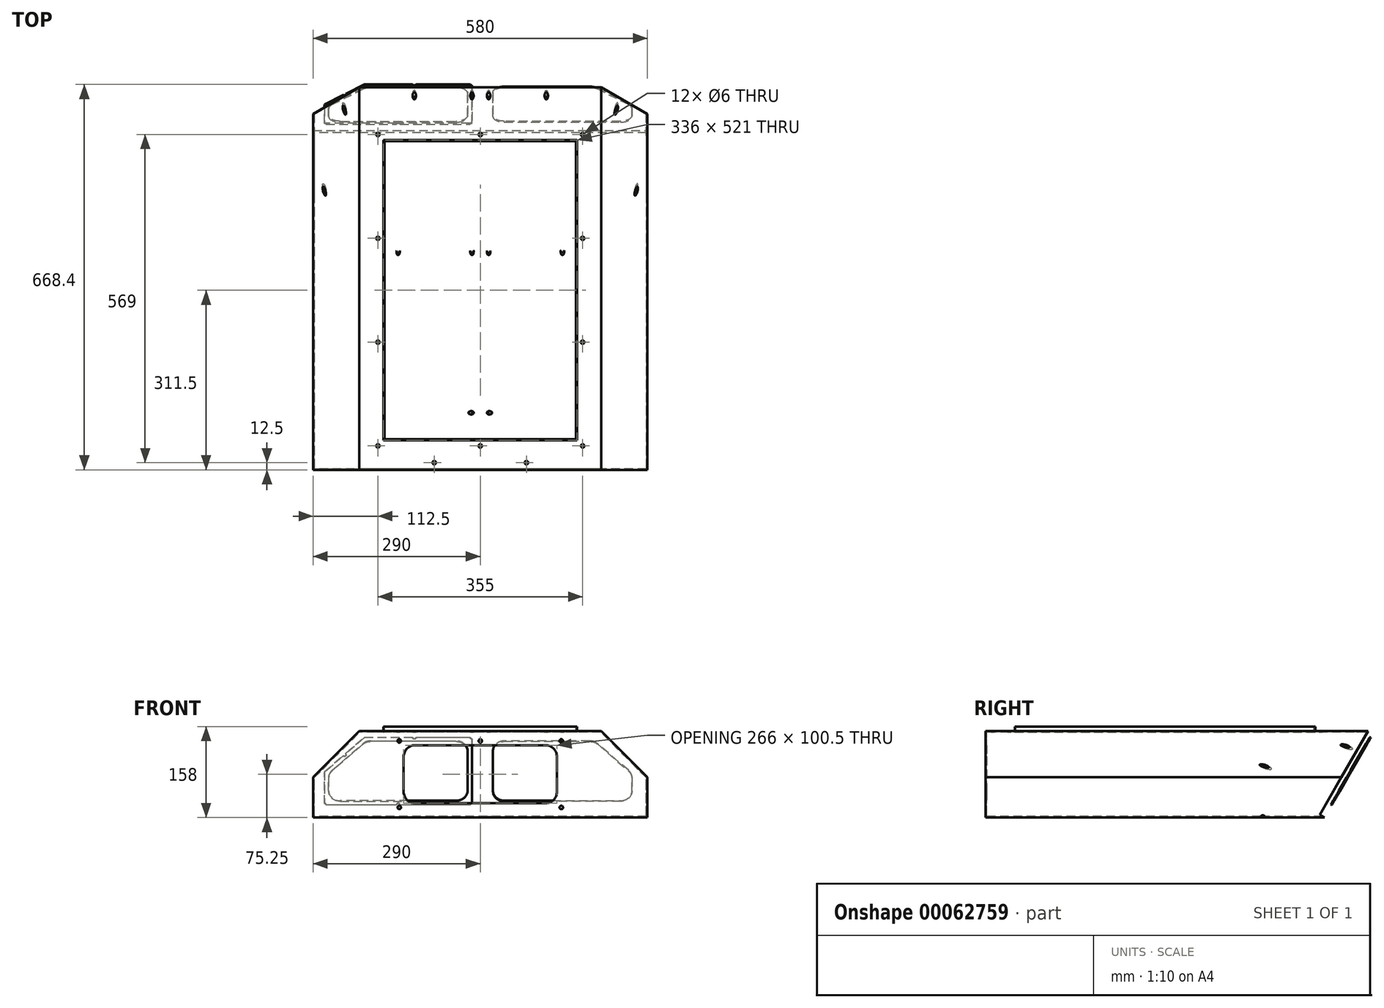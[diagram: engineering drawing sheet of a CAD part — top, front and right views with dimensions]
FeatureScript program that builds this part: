
annotation { "Feature Type Name" : "Feature", "Feature Type Description" : "" }
export const myFeature = defineFeature(function(context is Context, id is Id, definition is map)
    precondition{}
    {
        {
            var Q0;
            Q0=qCreatedBy(makeId("Front.planeOp"),FACE);
            var sketch = newSketch(context, id + "F0", { "sketchPlane" : qUnion([Q0])});
            skLineSegment(sketch, "E0", {"start": v(0, 0) * mm, "end": v(290, 0) * mm});
            skLineSegment(sketch, "E1", {"start": v(290, 0) * mm, "end": v(290, 70) * mm});
            skLineSegment(sketch, "E2", {"start": v(290, 70) * mm, "end": v(210, 150) * mm});
            skLineSegment(sketch, "E3", {"start": v(210, 150) * mm, "end": v(0, 150) * mm});
            skLineSegment(sketch, "E4", {"start": v(0, 150) * mm, "end": v(0, 0) * mm, "construction": true});
            skLineSegment(sketch, "E5.MirrorCS", {"start": v(-210, 150) * mm, "end": v(0, 150) * mm});
            skLineSegment(sketch, "E6.MirrorCS", {"start": v(-290, 70) * mm, "end": v(-210, 150) * mm});
            skLineSegment(sketch, "E7.MirrorCS", {"start": v(-290, 0) * mm, "end": v(-290, 70) * mm});
            skLineSegment(sketch, "E8.MirrorCS", {"start": v(0, 0) * mm, "end": v(-290, 0) * mm});
            skSolve(sketch);
        }
        {
            var Q0;
            Q0=makeQuery(id+"F0.imprint","IMPRINT",FACE,{"disambiguationData":[TD([[makeQuery(id+"F0.imprint","IMPRINT",EDGE,{"derivedFrom":sQuery(id+"F0.wireOp",EDGE,"E0")}),1.0]])]});
            extrude(context, id + "F1", {"entities" : qUnion([Q0]), "oppositeDirection" : true, "depth" : 675 * mm});
        }
        {
            var Q0;
            Q0=qCreatedBy(makeId("Right.planeOp"),FACE);
            var sketch = newSketch(context, id + "F2", { "sketchPlane" : qUnion([Q0])});
            skPoint(sketch, "E9.0", {"position": v(675, 150) * mm});
            skLineSegment(sketch, "E10", {"start": v(675, 150) * mm, "end": v(588.4, 0) * mm});
            skLineSegment(sketch, "E11.0", {"start": v(675, 0) * mm, "end": v(675, 70) * mm});
            skLineSegment(sketch, "E12.0", {"start": v(675, 70) * mm, "end": v(675, 150) * mm});
            skLineSegment(sketch, "E13", {"start": v(588.4, 0) * mm, "end": v(675, 0) * mm});
            skSolve(sketch);
        }
        {
            var Q0;
            Q0=qSketchRegion(id+"F2",true);
            extrude(context, id + "F3", {"entities" : qUnion([Q0]), "operationType" : NewBodyOperationType.REMOVE, "endBound" : BoundingType.THROUGH_ALL, "oppositeDirection" : true, "depth" : 25 * mm, "hasSecondDirection" : true, "secondDirectionBound" : SecondDirectionBoundingType.THROUGH_ALL, "secondDirectionOppositeDirection" : false, "secondDirectionDepth" : 25 * mm});
        }
        {
            var Q0;
            Q0=makeQuery(id+"F1.opExtrude","SWEPT_FACE",FACE,{"disambiguationData":[OSD([sQuery(id+"F0.wireOp",EDGE,"E3"),sQuery(id+"F0.wireOp",EDGE,"E5.MirrorCS")])]});
            var Q1;
            Q1=makeQuery(id+"F1.opExtrude","SWEPT_BODY",BODY,{"disambiguationData":[OSD([sQuery(id+"F0.wireOp",EDGE,"E0"),sQuery(id+"F0.wireOp",EDGE,"E1"),sQuery(id+"F0.wireOp",EDGE,"E2"),sQuery(id+"F0.wireOp",EDGE,"E3"),sQuery(id+"F0.wireOp",EDGE,"E5.MirrorCS"),sQuery(id+"F0.wireOp",EDGE,"E6.MirrorCS"),sQuery(id+"F0.wireOp",EDGE,"E7.MirrorCS"),sQuery(id+"F0.wireOp",EDGE,"E8.MirrorCS")])]});
            shell(context, id + "F4", {"isHollow" : true, "entities" : qUnion([Q0]), "parts" : qUnion([Q1]), "thickness" : 2 * mm});
        }
        {
            var Q0;
            Q0=makeQuery(id+"F1.opExtrude","CAP_FACE",FACE,{"disambiguationData":[OSD([sQuery(id+"F0.wireOp",EDGE,"E0"),sQuery(id+"F0.wireOp",EDGE,"E1"),sQuery(id+"F0.wireOp",EDGE,"E2"),sQuery(id+"F0.wireOp",EDGE,"E3"),sQuery(id+"F0.wireOp",EDGE,"E5.MirrorCS"),sQuery(id+"F0.wireOp",EDGE,"E6.MirrorCS"),sQuery(id+"F0.wireOp",EDGE,"E7.MirrorCS"),sQuery(id+"F0.wireOp",EDGE,"E8.MirrorCS")])],"isStart":true});
            var sketch = newSketch(context, id + "F5", { "sketchPlane" : qUnion([Q0])});
            skLineSegment(sketch, "E14.bottom", {"start": v(-113, 125.5) * mm, "end": v(113, 125.5) * mm});
            skLineSegment(sketch, "E14.top", {"start": v(-113, 25) * mm, "end": v(113, 25) * mm});
            skLineSegment(sketch, "E14.left", {"start": v(-133, 105.5) * mm, "end": v(-133, 45) * mm});
            skLineSegment(sketch, "E14.right", {"start": v(133, 105.5) * mm, "end": v(133, 45) * mm});
            skLineSegment(sketch, "E15", {"start": v(0, 0) * mm, "end": v(0, 150) * mm, "construction": true});
            skPoint(sketch, "E15.endSnap0", {"position": v(0, 25) * mm});
            skLineSegment(sketch, "E16", {"start": v(-140.5, 17.5) * mm, "end": v(178.16, 17.5) * mm, "construction": true});
            skLineSegment(sketch, "E17", {"start": v(140.5, 17.5) * mm, "end": v(140.5, 133) * mm, "construction": true});
            skLineSegment(sketch, "E18", {"start": v(140.5, 133) * mm, "end": v(-140.5, 133) * mm, "construction": true});
            skLineSegment(sketch, "E19", {"start": v(-140.5, 133) * mm, "end": v(-140.5, 17.5) * mm, "construction": true});
            skPoint(sketch, "E20.visualSharp", {"position": v(-133, 125.5) * mm});
            skArc(sketch, "E20.filletArc", {"start": v(-113, 125.5) * mm, "mid": v(-127.14, 119.64) * mm, "end": v(-133, 105.5) * mm});
            skPoint(sketch, "E21.visualSharp", {"position": v(-133, 25) * mm});
            skArc(sketch, "E21.filletArc", {"start": v(-133, 45) * mm, "mid": v(-127.14, 30.86) * mm, "end": v(-113, 25) * mm});
            skPoint(sketch, "E22.visualSharp", {"position": v(133, 25) * mm});
            skArc(sketch, "E22.filletArc", {"start": v(113, 25) * mm, "mid": v(127.14, 30.86) * mm, "end": v(133, 45) * mm});
            skPoint(sketch, "E23.visualSharp", {"position": v(133, 125.5) * mm});
            skArc(sketch, "E23.filletArc", {"start": v(133, 105.5) * mm, "mid": v(127.14, 119.64) * mm, "end": v(113, 125.5) * mm});
            skPoint(sketch, "E24", {"position": v(0, 133) * mm});
            skPoint(sketch, "E25", {"position": v(0, 17.5) * mm});
            skSolve(sketch);
        }
        {
            var Q0;
            Q0=makeQuery(id+"F5.imprint","IMPRINT",FACE,{"disambiguationData":[TD([[makeQuery(id+"F5.imprint","IMPRINT",EDGE,{"derivedFrom":sQuery(id+"F5.wireOp",EDGE,"E14.bottom")}),-1.0]])]});
            extrude(context, id + "F6", {"entities" : qUnion([Q0]), "operationType" : NewBodyOperationType.REMOVE, "oppositeDirection" : true, "depth" : 10 * mm});
        }
        {
            var Q0;
            Q0=sQuery(id+"F5.wireOp",VERTEX,"E19.start");
            var Q1;
            Q1=sQuery(id+"F5.wireOp",VERTEX,"E24");
            var Q2;
            Q2=sQuery(id+"F5.wireOp",VERTEX,"E18.start");
            var Q3;
            Q3=sQuery(id+"F5.wireOp",VERTEX,"E17.start");
            var Q4;
            Q4=sQuery(id+"F5.wireOp",VERTEX,"E16.start");
            var Q5;
            Q5=makeQuery(id+"F1.opExtrude","SWEPT_BODY",BODY,{"disambiguationData":[OSD([sQuery(id+"F0.wireOp",EDGE,"E0"),sQuery(id+"F0.wireOp",EDGE,"E1"),sQuery(id+"F0.wireOp",EDGE,"E2"),sQuery(id+"F0.wireOp",EDGE,"E3"),sQuery(id+"F0.wireOp",EDGE,"E5.MirrorCS"),sQuery(id+"F0.wireOp",EDGE,"E6.MirrorCS"),sQuery(id+"F0.wireOp",EDGE,"E7.MirrorCS"),sQuery(id+"F0.wireOp",EDGE,"E8.MirrorCS")])]});
            hole(context, id + "F7", {"style" : HoleStyle.SIMPLE, "holeDiameter" : 6 * mm, "endStyle" : HoleEndStyle.BLIND, "holeDepth" : 10 * mm, "locations" : qUnion([Q0, Q1, Q2, Q3, Q4]), "scope" : qUnion([Q5])});
        }
        {
            var Q0;
            Q0=makeQuery(id+"F3.boolean.opBoolean","COPY",FACE,{"derivedFrom":makeQuery(id+"F3.opExtrude","SWEPT_FACE",FACE,{"disambiguationData":[OSD([sQuery(id+"F2.wireOp",EDGE,"E10")])]})});
            var sketch = newSketch(context, id + "F8", { "sketchPlane" : qUnion([Q0])});
            skLineSegment(sketch, "E26", {"start": v(0, 467.4) * mm, "end": v(0, 294.2) * mm, "construction": true});
            skLineSegment(sketch, "E27", {"start": v(42, 446.7) * mm, "end": v(189.72, 446.7) * mm});
            skLineSegment(sketch, "E28", {"start": v(203.86, 440.84) * mm, "end": v(257.14, 387.56) * mm});
            skLineSegment(sketch, "E29", {"start": v(263, 373.41) * mm, "end": v(263, 346.7) * mm});
            skLineSegment(sketch, "E30", {"start": v(243, 326.7) * mm, "end": v(42, 326.7) * mm});
            skLineSegment(sketch, "E31", {"start": v(22, 426.7) * mm, "end": v(22, 346.7) * mm});
            skLineSegment(sketch, "E32", {"start": v(14.5, 454.2) * mm, "end": v(14.5, 319.2) * mm});
            skLineSegment(sketch, "E33", {"start": v(14.5, 319.2) * mm, "end": v(270.5, 319.2) * mm});
            skLineSegment(sketch, "E34", {"start": v(270.5, 319.2) * mm, "end": v(270.5, 384.8) * mm});
            skLineSegment(sketch, "E35", {"start": v(14.5, 454.2) * mm, "end": v(201.1, 454.2) * mm});
            skLineSegment(sketch, "E36.0", {"start": v(201.1, 454.2) * mm, "end": v(270.5, 384.8) * mm});
            skPoint(sketch, "E37.visualSharp", {"position": v(198, 446.7) * mm});
            skArc(sketch, "E37.filletArc", {"start": v(203.86, 440.84) * mm, "mid": v(197.37, 445.18) * mm, "end": v(189.72, 446.7) * mm});
            skPoint(sketch, "E38.visualSharp", {"position": v(263, 381.7) * mm});
            skArc(sketch, "E38.filletArc", {"start": v(263, 373.41) * mm, "mid": v(261.48, 381.07) * mm, "end": v(257.14, 387.56) * mm});
            skPoint(sketch, "E39.visualSharp", {"position": v(263, 326.7) * mm});
            skArc(sketch, "E39.filletArc", {"start": v(243, 326.7) * mm, "mid": v(257.14, 332.56) * mm, "end": v(263, 346.7) * mm});
            skPoint(sketch, "E40.visualSharp", {"position": v(22, 326.7) * mm});
            skArc(sketch, "E40.filletArc", {"start": v(22, 346.7) * mm, "mid": v(27.86, 332.56) * mm, "end": v(42, 326.7) * mm});
            skPoint(sketch, "E41.visualSharp", {"position": v(22, 446.7) * mm});
            skArc(sketch, "E41.filletArc", {"start": v(42, 446.7) * mm, "mid": v(27.86, 440.84) * mm, "end": v(22, 426.7) * mm});
            skPoint(sketch, "E42", {"position": v(235.8, 419.5) * mm});
            skPoint(sketch, "E43", {"position": v(114.5, 454.2) * mm});
            skPoint(sketch, "E44", {"position": v(142.5, 319.2) * mm});
            skArc(sketch, "E45.MirrorCS", {"start": v(-42, 446.7) * mm, "mid": v(-27.86, 440.84) * mm, "end": v(-22, 426.7) * mm});
            skPoint(sketch, "E46.MirrorP", {"position": v(-114.5, 454.2) * mm});
            skLineSegment(sketch, "E47.MirrorCS", {"start": v(-22, 426.7) * mm, "end": v(-22, 346.7) * mm});
            skArc(sketch, "E48.MirrorCS", {"start": v(-22, 346.7) * mm, "mid": v(-27.86, 332.56) * mm, "end": v(-42, 326.7) * mm});
            skLineSegment(sketch, "E49.MirrorCS", {"start": v(-243, 326.7) * mm, "end": v(-42, 326.7) * mm});
            skArc(sketch, "E50.MirrorCS", {"start": v(-243, 326.7) * mm, "mid": v(-257.14, 332.56) * mm, "end": v(-263, 346.7) * mm});
            skLineSegment(sketch, "E51.MirrorCS", {"start": v(-263, 373.41) * mm, "end": v(-263, 346.7) * mm});
            skArc(sketch, "E52.MirrorCS", {"start": v(-263, 373.41) * mm, "mid": v(-261.48, 381.07) * mm, "end": v(-257.14, 387.56) * mm});
            skLineSegment(sketch, "E53.MirrorCS", {"start": v(-203.86, 440.84) * mm, "end": v(-257.14, 387.56) * mm});
            skLineSegment(sketch, "E54.MirrorCS", {"start": v(-42, 446.7) * mm, "end": v(-189.72, 446.7) * mm});
            skArc(sketch, "E55.MirrorCS", {"start": v(-203.86, 440.84) * mm, "mid": v(-197.37, 445.18) * mm, "end": v(-189.72, 446.7) * mm});
            skPoint(sketch, "E56.MirrorP", {"position": v(-142.5, 319.2) * mm});
            skPoint(sketch, "E57", {"position": v(14.5, 454.2) * mm});
            skPoint(sketch, "E58", {"position": v(14.5, 319.2) * mm});
            skPoint(sketch, "E59", {"position": v(270.5, 319.2) * mm});
            skPoint(sketch, "E60.MirrorP", {"position": v(-14.5, 454.2) * mm});
            skPoint(sketch, "E61.MirrorP", {"position": v(-14.5, 319.2) * mm});
            skPoint(sketch, "E62.MirrorP", {"position": v(-270.5, 319.2) * mm});
            skPoint(sketch, "E63.MirrorP", {"position": v(-235.8, 419.5) * mm});
            skSolve(sketch);
        }
        {
            var Q0;
            Q0=makeQuery(id+"F8.imprint","IMPRINT",FACE,{"disambiguationData":[TD([[makeQuery(id+"F8.imprint","IMPRINT",EDGE,{"derivedFrom":sQuery(id+"F8.wireOp",EDGE,"E27")}),-1.0]])]});
            var Q1;
            Q1=makeQuery(id+"F8.imprint","IMPRINT",FACE,{"disambiguationData":[TD([[makeQuery(id+"F8.imprint","IMPRINT",EDGE,{"derivedFrom":sQuery(id+"F8.wireOp",EDGE,"E45.MirrorCS")}),-1.0]])]});
            extrude(context, id + "F9", {"entities" : qUnion([Q0, Q1]), "operationType" : NewBodyOperationType.REMOVE, "oppositeDirection" : true, "depth" : 10 * mm});
        }
        {
            var Q0;
            Q0=sQuery(id+"F8.wireOp",VERTEX,"E46.MirrorP");
            var Q1;
            Q1=sQuery(id+"F8.wireOp",VERTEX,"E60.MirrorP");
            var Q2;
            Q2=sQuery(id+"F8.wireOp",VERTEX,"E57");
            var Q3;
            Q3=sQuery(id+"F8.wireOp",VERTEX,"E43");
            var Q4;
            Q4=sQuery(id+"F8.wireOp",VERTEX,"E42");
            var Q5;
            Q5=sQuery(id+"F8.wireOp",VERTEX,"E59");
            var Q6;
            Q6=sQuery(id+"F8.wireOp",VERTEX,"E58");
            var Q7;
            Q7=sQuery(id+"F8.wireOp",VERTEX,"E61.MirrorP");
            var Q8;
            Q8=sQuery(id+"F8.wireOp",VERTEX,"E56.MirrorP");
            var Q9;
            Q9=sQuery(id+"F8.wireOp",VERTEX,"E62.MirrorP");
            var Q10;
            Q10=sQuery(id+"F8.wireOp",VERTEX,"E63.MirrorP");
            var Q11;
            Q11=sQuery(id+"F8.wireOp",VERTEX,"E44");
            var Q12;
            Q12=makeQuery(id+"F1.opExtrude","SWEPT_BODY",BODY,{"disambiguationData":[OSD([sQuery(id+"F0.wireOp",EDGE,"E0"),sQuery(id+"F0.wireOp",EDGE,"E1"),sQuery(id+"F0.wireOp",EDGE,"E2"),sQuery(id+"F0.wireOp",EDGE,"E3"),sQuery(id+"F0.wireOp",EDGE,"E5.MirrorCS"),sQuery(id+"F0.wireOp",EDGE,"E6.MirrorCS"),sQuery(id+"F0.wireOp",EDGE,"E7.MirrorCS"),sQuery(id+"F0.wireOp",EDGE,"E8.MirrorCS")])]});
            hole(context, id + "F10", {"style" : HoleStyle.SIMPLE, "holeDiameter" : 6 * mm, "endStyle" : HoleEndStyle.BLIND, "holeDepth" : 10 * mm, "locations" : qUnion([Q0, Q1, Q2, Q3, Q4, Q5, Q6, Q7, Q8, Q9, Q10, Q11]), "scope" : qUnion([Q12])});
        }
        {
            var Q0;
            Q0=makeQuery(id+"F1.opExtrude","SWEPT_FACE",FACE,{"disambiguationData":[OSD([sQuery(id+"F0.wireOp",EDGE,"E3"),sQuery(id+"F0.wireOp",EDGE,"E5.MirrorCS")])]});
            var sketch = newSketch(context, id + "F11", { "sketchPlane" : qUnion([Q0])});
            skLineSegment(sketch, "E64", {"start": v(-166, 570) * mm, "end": v(-166, 53) * mm});
            skLineSegment(sketch, "E65", {"start": v(-166, 53) * mm, "end": v(166, 53) * mm});
            skLineSegment(sketch, "E66", {"start": v(166, 53) * mm, "end": v(166, 570) * mm});
            skLineSegment(sketch, "E67", {"start": v(166, 570) * mm, "end": v(-166, 570) * mm});
            skLineSegment(sketch, "E68.0", {"start": v(177.5, 581.5) * mm, "end": v(-177.5, 581.5) * mm, "construction": true});
            skLineSegment(sketch, "E68.1", {"start": v(177.5, 41.5) * mm, "end": v(177.5, 581.5) * mm, "construction": true});
            skLineSegment(sketch, "E68.2", {"start": v(-177.5, 41.5) * mm, "end": v(177.5, 41.5) * mm, "construction": true});
            skLineSegment(sketch, "E68.3", {"start": v(-177.5, 581.5) * mm, "end": v(-177.5, 41.5) * mm, "construction": true});
            skLineSegment(sketch, "E69", {"start": v(0, 53) * mm, "end": v(0, 0) * mm, "construction": true});
            skPoint(sketch, "E70", {"position": v(-177.5, 581.5) * mm});
            skPoint(sketch, "E71", {"position": v(177.5, 581.5) * mm});
            skPoint(sketch, "E72", {"position": v(177.5, 41.5) * mm});
            skPoint(sketch, "E73", {"position": v(-177.5, 41.5) * mm});
            skPoint(sketch, "E74", {"position": v(0, 581.5) * mm});
            skPoint(sketch, "E75", {"position": v(0, 41.5) * mm});
            skPoint(sketch, "E76", {"position": v(-177.5, 221.5) * mm});
            skPoint(sketch, "E77", {"position": v(-177.5, 401.5) * mm});
            skLineSegment(sketch, "E78", {"start": v(0, 53) * mm, "end": v(0, 570) * mm, "construction": true});
            skPoint(sketch, "E79.MirrorP", {"position": v(177.5, 221.5) * mm});
            skPoint(sketch, "E80.MirrorP", {"position": v(177.5, 401.5) * mm});
            skLineSegment(sketch, "E81", {"start": v(-80, 12.5) * mm, "end": v(80, 12.5) * mm});
            skPoint(sketch, "E82", {"position": v(0, 12.5) * mm});
            skPoint(sketch, "E83", {"position": v(-80, 12.5) * mm});
            skPoint(sketch, "E84", {"position": v(80, 12.5) * mm});
            skSolve(sketch);
        }
        {
            var Q0;
            Q0=makeQuery(id+"F11.imprint","IMPRINT",FACE,{"disambiguationData":[TD([[makeQuery(id+"F11.imprint","IMPRINT",EDGE,{"derivedFrom":sQuery(id+"F11.wireOp",EDGE,"E64")}),1.0]])]});
            extrude(context, id + "F12", {"entities" : qUnion([Q0]), "operationType" : NewBodyOperationType.REMOVE, "oppositeDirection" : true, "depth" : 10 * mm});
        }
        {
            var Q0;
            Q0=makeQuery(id+"F1.opExtrude","SWEPT_FACE",FACE,{"disambiguationData":[OSD([sQuery(id+"F0.wireOp",EDGE,"E3"),sQuery(id+"F0.wireOp",EDGE,"E5.MirrorCS")])]});
            var sketch = newSketch(context, id + "F13", { "sketchPlane" : qUnion([Q0])});
            skLineSegment(sketch, "E85.0", {"start": v(168, 572) * mm, "end": v(-168, 572) * mm});
            skLineSegment(sketch, "E85.1", {"start": v(168, 51) * mm, "end": v(168, 572) * mm});
            skLineSegment(sketch, "E85.2", {"start": v(-168, 51) * mm, "end": v(168, 51) * mm});
            skLineSegment(sketch, "E85.3", {"start": v(-168, 572) * mm, "end": v(-168, 51) * mm});
            skSolve(sketch);
        }
        {
            var Q0;
            Q0=makeQuery(id+"F13.imprint","IMPRINT",FACE,{"disambiguationData":[TD([[makeQuery(id+"F13.imprint","IMPRINT",EDGE,{"derivedFrom":sQuery(id+"F13.wireOp",EDGE,"E85.0")}),1.0]])]});
            extrude(context, id + "F14", {"entities" : qUnion([Q0]), "operationType" : NewBodyOperationType.ADD, "depth" : 8 * mm});
        }
        {
            var Q0;
            Q0=makeQuery(id+"F14.opExtrude","CAP_EDGE",EDGE,{"disambiguationData":[OSD([sQuery(id+"F13.wireOp",EDGE,"E85.1")])],"isStart":true});
            var Q1;
            Q1=makeQuery(id+"F14.opExtrude","CAP_EDGE",EDGE,{"disambiguationData":[OSD([sQuery(id+"F13.wireOp",EDGE,"E85.0")])],"isStart":true});
            var Q2;
            Q2=makeQuery(id+"F14.opExtrude","CAP_EDGE",EDGE,{"disambiguationData":[OSD([sQuery(id+"F13.wireOp",EDGE,"E85.2")])],"isStart":true});
            var Q3;
            Q3=makeQuery(id+"F14.opExtrude","CAP_EDGE",EDGE,{"disambiguationData":[OSD([sQuery(id+"F13.wireOp",EDGE,"E85.3")])],"isStart":true});
            var Q4;
            Q4=makeQuery(id+"F12.boolean.opBoolean","INTERSECT",EDGE,{"derivedFrom":[makeQuery(id+"F4.opShell","OFFSET_FACE",FACE,{"disambiguationData":[OSD([sQuery(id+"F0.wireOp",EDGE,"E3"),sQuery(id+"F0.wireOp",EDGE,"E5.MirrorCS")])]}),makeQuery(id+"F12.opExtrude","SWEPT_FACE",FACE,{"disambiguationData":[OSD([sQuery(id+"F11.wireOp",EDGE,"E65")])]})]});
            var Q5;
            Q5=makeQuery(id+"F12.boolean.opBoolean","INTERSECT",EDGE,{"derivedFrom":[makeQuery(id+"F4.opShell","OFFSET_FACE",FACE,{"disambiguationData":[OSD([sQuery(id+"F0.wireOp",EDGE,"E3"),sQuery(id+"F0.wireOp",EDGE,"E5.MirrorCS")])]}),makeQuery(id+"F12.opExtrude","SWEPT_FACE",FACE,{"disambiguationData":[OSD([sQuery(id+"F11.wireOp",EDGE,"E64")])]})]});
            var Q6;
            Q6=makeQuery(id+"F12.boolean.opBoolean","INTERSECT",EDGE,{"derivedFrom":[makeQuery(id+"F4.opShell","OFFSET_FACE",FACE,{"disambiguationData":[OSD([sQuery(id+"F0.wireOp",EDGE,"E3"),sQuery(id+"F0.wireOp",EDGE,"E5.MirrorCS")])]}),makeQuery(id+"F12.opExtrude","SWEPT_FACE",FACE,{"disambiguationData":[OSD([sQuery(id+"F11.wireOp",EDGE,"E66")])]})]});
            var Q7;
            Q7=makeQuery(id+"F12.boolean.opBoolean","INTERSECT",EDGE,{"derivedFrom":[makeQuery(id+"F4.opShell","OFFSET_FACE",FACE,{"disambiguationData":[OSD([sQuery(id+"F0.wireOp",EDGE,"E3"),sQuery(id+"F0.wireOp",EDGE,"E5.MirrorCS")])]}),makeQuery(id+"F12.opExtrude","SWEPT_FACE",FACE,{"disambiguationData":[OSD([sQuery(id+"F11.wireOp",EDGE,"E67")])]})]});
            fillet(context, id + "F15", {"entities" : qUnion([Q0, Q1, Q2, Q3, Q4, Q5, Q6, Q7]), "radius" : 2 * mm, "tangentPropagation" : true, "allowEdgeOverflow" : false});
        }
        {
            var Q0;
            Q0=sQuery(id+"F11.wireOp",VERTEX,"E70");
            var Q1;
            Q1=sQuery(id+"F11.wireOp",VERTEX,"E77");
            var Q2;
            Q2=sQuery(id+"F11.wireOp",VERTEX,"E76");
            var Q3;
            Q3=sQuery(id+"F11.wireOp",VERTEX,"E73");
            var Q4;
            Q4=sQuery(id+"F11.wireOp",VERTEX,"E75");
            var Q5;
            Q5=sQuery(id+"F11.wireOp",VERTEX,"E72");
            var Q6;
            Q6=sQuery(id+"F11.wireOp",VERTEX,"E79.MirrorP");
            var Q7;
            Q7=sQuery(id+"F11.wireOp",VERTEX,"E71");
            var Q8;
            Q8=sQuery(id+"F11.wireOp",VERTEX,"E74");
            var Q9;
            Q9=sQuery(id+"F11.wireOp",VERTEX,"E80.MirrorP");
            var Q10;
            Q10=sQuery(id+"F11.wireOp",VERTEX,"E83");
            var Q11;
            Q11=sQuery(id+"F11.wireOp",VERTEX,"E84");
            var Q12;
            Q12=makeQuery(id+"F1.opExtrude","SWEPT_BODY",BODY,{"disambiguationData":[OSD([sQuery(id+"F0.wireOp",EDGE,"E0"),sQuery(id+"F0.wireOp",EDGE,"E1"),sQuery(id+"F0.wireOp",EDGE,"E2"),sQuery(id+"F0.wireOp",EDGE,"E3"),sQuery(id+"F0.wireOp",EDGE,"E5.MirrorCS"),sQuery(id+"F0.wireOp",EDGE,"E6.MirrorCS"),sQuery(id+"F0.wireOp",EDGE,"E7.MirrorCS"),sQuery(id+"F0.wireOp",EDGE,"E8.MirrorCS")])]});
            hole(context, id + "F16", {"style" : HoleStyle.SIMPLE, "holeDiameter" : 6 * mm, "endStyle" : HoleEndStyle.BLIND, "holeDepth" : 10 * mm, "locations" : qUnion([Q0, Q1, Q2, Q3, Q4, Q5, Q6, Q7, Q8, Q9, Q10, Q11]), "scope" : qUnion([Q12])});
        }
        {
            var Q0;
            Q0=makeQuery(id+"F1.opExtrude","SWEPT_FACE",FACE,{"disambiguationData":[OSD([sQuery(id+"F0.wireOp",EDGE,"E2")])]});
            var sketch = newSketch(context, id + "F17", { "sketchPlane" : qUnion([Q0])});
            skLineSegment(sketch, "E86", {"start": v(99, 0) * mm, "end": v(99, 12.5) * mm, "construction": true});
            skPoint(sketch, "E87", {"position": v(99, 12.5) * mm});
            skSolve(sketch);
        }
        {
            var Q0;
            Q0=sQuery(id+"F17.wireOp",VERTEX,"E87");
            var Q1;
            Q1=makeQuery(id+"F1.opExtrude","SWEPT_BODY",BODY,{"disambiguationData":[OSD([sQuery(id+"F0.wireOp",EDGE,"E0"),sQuery(id+"F0.wireOp",EDGE,"E1"),sQuery(id+"F0.wireOp",EDGE,"E2"),sQuery(id+"F0.wireOp",EDGE,"E3"),sQuery(id+"F0.wireOp",EDGE,"E5.MirrorCS"),sQuery(id+"F0.wireOp",EDGE,"E6.MirrorCS"),sQuery(id+"F0.wireOp",EDGE,"E7.MirrorCS"),sQuery(id+"F0.wireOp",EDGE,"E8.MirrorCS")])]});
            hole(context, id + "F18", {"style" : HoleStyle.SIMPLE, "holeDiameter" : 6 * mm, "endStyle" : HoleEndStyle.BLIND, "holeDepth" : 10 * mm, "locations" : qUnion([Q0]), "scope" : qUnion([Q1])});
        }
        {
            var Q0;
            Q0=makeQuery(id+"F1.opExtrude","SWEPT_FACE",FACE,{"disambiguationData":[OSD([sQuery(id+"F0.wireOp",EDGE,"E6.MirrorCS")])]});
            var sketch = newSketch(context, id + "F19", { "sketchPlane" : qUnion([Q0])});
            skLineSegment(sketch, "E88", {"start": v(-99, 0) * mm, "end": v(-99, 12.5) * mm, "construction": true});
            skPoint(sketch, "E89", {"position": v(-99, 12.5) * mm});
            skSolve(sketch);
        }
        {
            var Q0;
            Q0=sQuery(id+"F19.wireOp",VERTEX,"E89");
            var Q1;
            Q1=makeQuery(id+"F1.opExtrude","SWEPT_BODY",BODY,{"disambiguationData":[OSD([sQuery(id+"F0.wireOp",EDGE,"E0"),sQuery(id+"F0.wireOp",EDGE,"E1"),sQuery(id+"F0.wireOp",EDGE,"E2"),sQuery(id+"F0.wireOp",EDGE,"E3"),sQuery(id+"F0.wireOp",EDGE,"E5.MirrorCS"),sQuery(id+"F0.wireOp",EDGE,"E6.MirrorCS"),sQuery(id+"F0.wireOp",EDGE,"E7.MirrorCS"),sQuery(id+"F0.wireOp",EDGE,"E8.MirrorCS")])]});
            hole(context, id + "F20", {"style" : HoleStyle.SIMPLE, "holeDiameter" : 6 * mm, "endStyle" : HoleEndStyle.BLIND, "holeDepth" : 10 * mm, "locations" : qUnion([Q0]), "scope" : qUnion([Q1])});
        }
        {
            var Q0;
            Q0=makeQuery(id+"F1.opExtrude","SWEPT_FACE",FACE,{"disambiguationData":[OSD([sQuery(id+"F0.wireOp",EDGE,"E1")])]});
            var sketch = newSketch(context, id + "F21", { "sketchPlane" : qUnion([Q0])});
            skArc(sketch, "E90", {"start": v(484.9, 0) * mm, "mid": v(480.9, 4) * mm, "end": v(476.9, 0) * mm});
            skLineSegment(sketch, "E91.0", {"start": v(484.9, 0) * mm, "end": v(0, 0) * mm});
            skPoint(sketch, "E92.orphan", {"position": v(588.4, 0) * mm});
            skSolve(sketch);
        }
        {
            var Q0;
            Q0=qSketchRegion(id+"F21",true);
            extrude(context, id + "F22", {"entities" : qUnion([Q0]), "operationType" : NewBodyOperationType.REMOVE, "oppositeDirection" : true, "depth" : 2 * mm});
        }
        {
            var Q0;
            Q0=makeQuery(id+"F1.opExtrude","SWEPT_FACE",FACE,{"disambiguationData":[OSD([sQuery(id+"F0.wireOp",EDGE,"E7.MirrorCS")])]});
            var sketch = newSketch(context, id + "F23", { "sketchPlane" : qUnion([Q0])});
            skArc(sketch, "E93", {"start": v(-476.9, 0) * mm, "mid": v(-480.9, 4) * mm, "end": v(-484.9, 0) * mm});
            skLineSegment(sketch, "E94.0", {"start": v(-484.9, 0) * mm, "end": v(-476.9, 0) * mm});
            skPoint(sketch, "E95.orphan", {"position": v(0, 0) * mm});
            skPoint(sketch, "E96.orphan", {"position": v(-588.4, 0) * mm});
            skSolve(sketch);
        }
        {
            var Q0;
            Q0=qSketchRegion(id+"F23",true);
            extrude(context, id + "F24", {"entities" : qUnion([Q0]), "operationType" : NewBodyOperationType.REMOVE, "oppositeDirection" : true, "depth" : 2 * mm});
        }
    });
